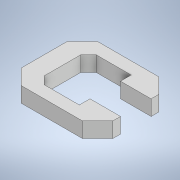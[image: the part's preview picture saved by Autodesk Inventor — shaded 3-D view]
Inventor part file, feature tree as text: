
AUTODESK INVENTOR PART (.ipt)
format: ipt  version: 2022.2 (Build 262287030, 287C)  size: 119,808 bytes
history: native  units: in
note: dims shown in document units (in); Inventor stores cm internally (conversion verified against a paired STEP export)
features: extrude x1, sketch x1
ambient origin geometry x8: Origin, YZ Plane, XZ Plane, XY Plane, X Axis, Y Axis, Z Axis, Center Point
bodies: Solid1 (feature_tree)
feature tree (2):
  extrude  "Extrusion1"  Depth=1.5in
  sketch  "Sketch1"  dims[d0=45.0deg d1=1.5in d2=1.25in d3=0.375in d4=0.2in d5=0.5in d6=0.2in d7=0.125in d8=0.3in d9=0.25in d10=1.25in d11=0.5in d12=0.25in d13=0.0in]
